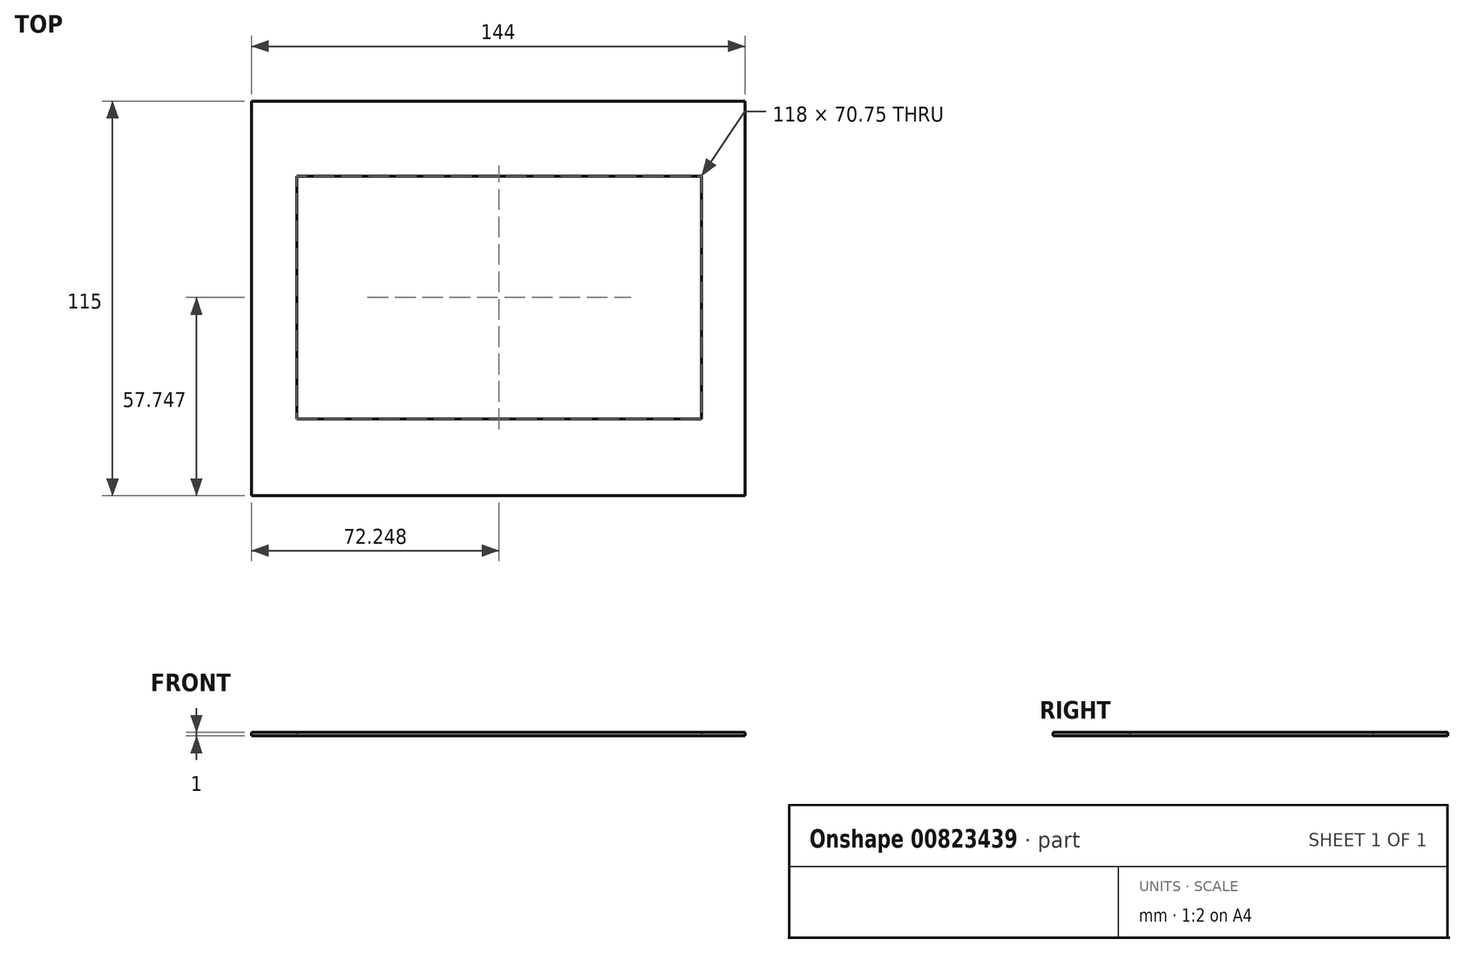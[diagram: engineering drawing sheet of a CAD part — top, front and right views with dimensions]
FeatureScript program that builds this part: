
annotation { "Feature Type Name" : "Feature", "Feature Type Description" : "" }
export const myFeature = defineFeature(function(context is Context, id is Id, definition is map)
    precondition{}
    {
        {
            var Q0;
            Q0=qCreatedBy(makeId("Top.planeOp"),FACE);
            var sketch = newSketch(context, id + "F0", { "sketchPlane" : qUnion([Q0])});
            skLineSegment(sketch, "E0.bottom", {"start": v(-71.07, 65.38) * mm, "end": v(72.93, 65.38) * mm});
            skLineSegment(sketch, "E0.top", {"start": v(-71.07, -49.62) * mm, "end": v(72.93, -49.62) * mm});
            skLineSegment(sketch, "E0.left", {"start": v(-71.07, 65.38) * mm, "end": v(-71.07, -49.62) * mm});
            skLineSegment(sketch, "E0.right", {"start": v(72.93, 65.38) * mm, "end": v(72.93, -49.62) * mm});
            skLineSegment(sketch, "E1.bottom", {"start": v(-57.82, 43.5) * mm, "end": v(60.18, 43.5) * mm});
            skLineSegment(sketch, "E1.top", {"start": v(-57.82, -27.25) * mm, "end": v(60.18, -27.25) * mm});
            skLineSegment(sketch, "E1.left", {"start": v(-57.82, 43.5) * mm, "end": v(-57.82, -27.25) * mm});
            skLineSegment(sketch, "E1.right", {"start": v(60.18, 43.5) * mm, "end": v(60.18, -27.25) * mm});
            skSolve(sketch);
        }
        {
            var Q0;
            Q0=makeQuery(id+"F0.imprint","IMPRINT",FACE,{"disambiguationData":[TD([[makeQuery(id+"F0.imprint","IMPRINT",EDGE,{"derivedFrom":sQuery(id+"F0.wireOp",EDGE,"E0.bottom")}),-1.0]])]});
            extrude(context, id + "F1", {"entities" : qUnion([Q0]), "depth" : 1 * mm, "offsetDistance" : 25 * mm});
        }
    });
